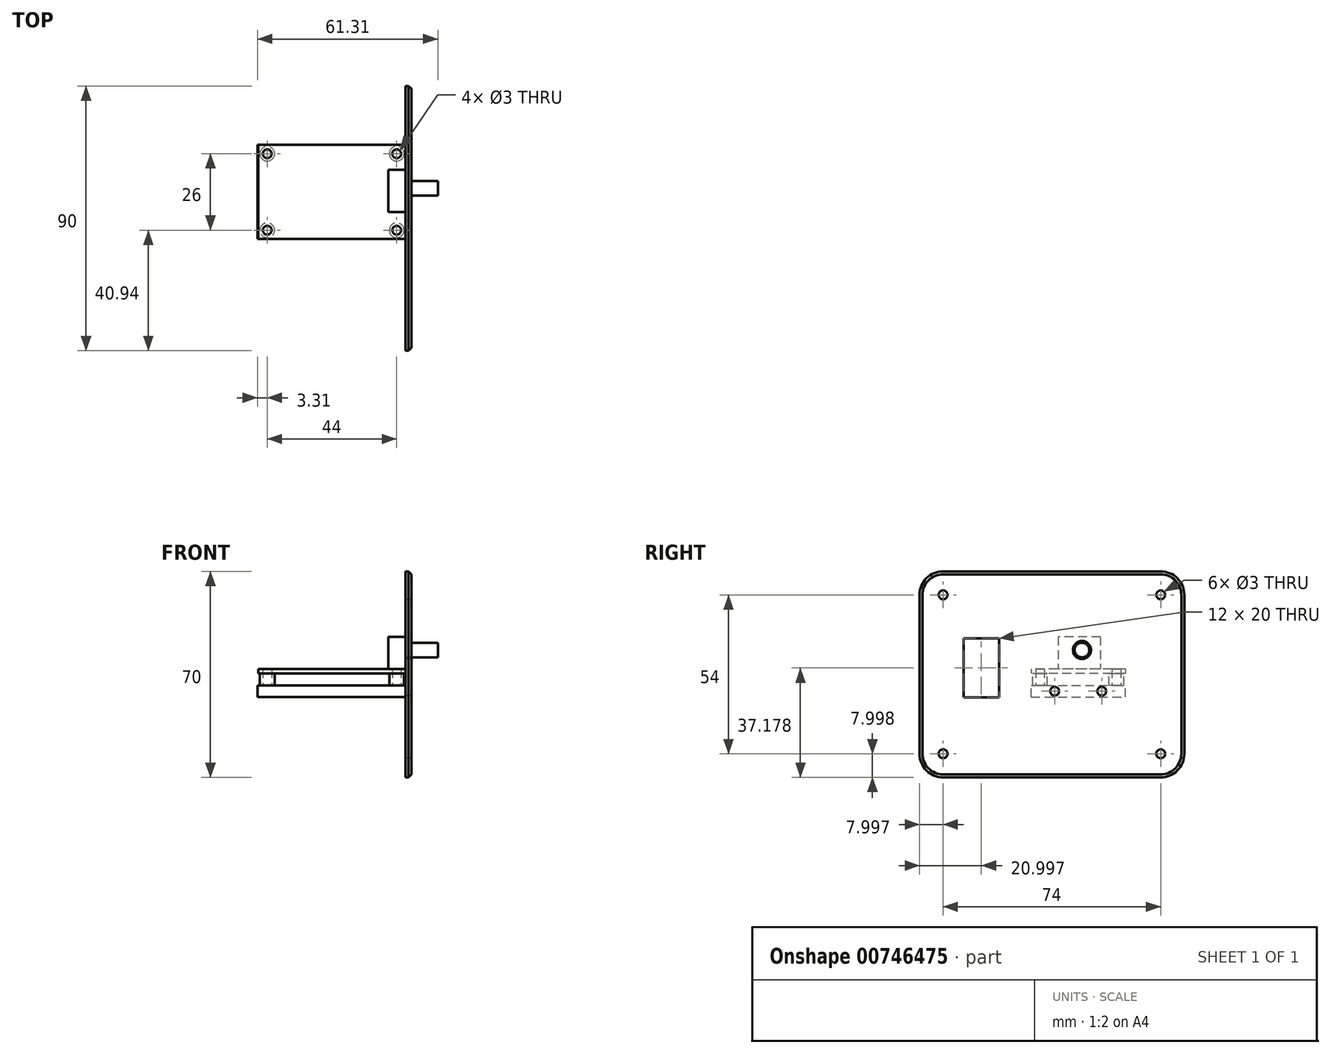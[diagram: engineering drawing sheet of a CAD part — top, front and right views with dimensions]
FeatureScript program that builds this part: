
annotation { "Feature Type Name" : "Feature", "Feature Type Description" : "" }
export const myFeature = defineFeature(function(context is Context, id is Id, definition is map)
    precondition{}
    {
        {
            var Q0;
            Q0=qCreatedBy(makeId("Top.planeOp"),FACE);
            var sketch = newSketch(context, id + "F0", { "sketchPlane" : qUnion([Q0])});
            skLineSegment(sketch, "E0.bottom", {"start": v(-13.65, 14.73) * mm, "end": v(36.35, 14.73) * mm});
            skLineSegment(sketch, "E0.top", {"start": v(-13.65, -17.27) * mm, "end": v(36.35, -17.27) * mm});
            skLineSegment(sketch, "E0.left", {"start": v(-13.65, 14.73) * mm, "end": v(-13.65, -17.27) * mm});
            skLineSegment(sketch, "E0.right", {"start": v(36.35, 14.73) * mm, "end": v(36.35, -17.27) * mm});
            skCircle(sketch, "E1", {"center": v(-10.65, 11.73) * mm, "radius": 1.5 * mm});
            skCircle(sketch, "E2", {"center": v(33.35, 11.73) * mm, "radius": 1.5 * mm});
            skCircle(sketch, "E3.0.1.0", {"center": v(-10.65, -14.27) * mm, "radius": 1.5 * mm});
            skCircle(sketch, "E3.0.1.1", {"center": v(33.35, -14.27) * mm, "radius": 1.5 * mm});
            skLineSegment(sketch, "E3.direction1", {"start": v(-10.65, 11.73) * mm, "end": v(12.25, 11.73) * mm, "construction": true});
            skLineSegment(sketch, "E3.direction2", {"start": v(-10.65, 11.73) * mm, "end": v(-10.65, -14.27) * mm, "construction": true});
            skSolve(sketch);
        }
        {
            var Q0;
            Q0=makeQuery(id+"F0.imprint","IMPRINT",FACE,{"disambiguationData":[TD([[makeQuery(id+"F0.imprint","IMPRINT",EDGE,{"derivedFrom":sQuery(id+"F0.wireOp",EDGE,"E0.bottom")}),-1.0]])]});
            extrude(context, id + "F1", {"entities" : qUnion([Q0]), "depth" : 1.5 * mm, "offsetDistance" : 25 * mm});
        }
        {
            var Q0;
            Q0=makeQuery(id+"F1.opExtrude","CAP_FACE",FACE,{"disambiguationData":[OSD([sQuery(id+"F0.wireOp",EDGE,"E0.bottom"),sQuery(id+"F0.wireOp",EDGE,"E0.top"),sQuery(id+"F0.wireOp",EDGE,"E0.left"),sQuery(id+"F0.wireOp",EDGE,"E0.right"),sQuery(id+"F0.wireOp",EDGE,"E1"),sQuery(id+"F0.wireOp",EDGE,"E2"),sQuery(id+"F0.wireOp",EDGE,"E3.0.1.0"),sQuery(id+"F0.wireOp",EDGE,"E3.0.1.1")])],"isStart":false});
            var sketch = newSketch(context, id + "F2", { "sketchPlane" : qUnion([Q0])});
            skLineSegment(sketch, "E4.bottom", {"start": v(36.35, 6.31) * mm, "end": v(30.58, 6.31) * mm});
            skLineSegment(sketch, "E4.top", {"start": v(36.35, -8.08) * mm, "end": v(30.58, -8.08) * mm});
            skLineSegment(sketch, "E4.left", {"start": v(36.35, 6.31) * mm, "end": v(36.35, -8.08) * mm});
            skLineSegment(sketch, "E4.right", {"start": v(30.58, 6.31) * mm, "end": v(30.58, -8.08) * mm});
            skSolve(sketch);
        }
        {
            var Q0;
            Q0 = qSketchRegion(id + "F2", true);
            extrude(context, id + "F3", {"entities" : qUnion([Q0]), "operationType" : NewBodyOperationType.ADD, "depth" : 11 * mm, "offsetDistance" : 25 * mm});
        }
        {
            var Q0;
            Q0=makeQuery(id+"F3.boolean.opBoolean","MERGE",FACE,{"derivedFrom":[makeQuery(id+"F1.opExtrude","SWEPT_FACE",FACE,{"disambiguationData":[OSD([sQuery(id+"F0.wireOp",EDGE,"E0.right")])]}),makeQuery(id+"F3.opExtrude","SWEPT_FACE",FACE,{"disambiguationData":[OSD([sQuery(id+"F2.wireOp",EDGE,"E4.left")])]})]});
            var sketch = newSketch(context, id + "F4", { "sketchPlane" : qUnion([Q0])});
            skCircle(sketch, "E5", {"center": v(0, 8) * mm, "radius": 2.5 * mm});
            skSolve(sketch);
        }
        {
            var Q0;
            Q0 = qSketchRegion(id + "F4", true);
            extrude(context, id + "F5", {"entities" : qUnion([Q0]), "operationType" : NewBodyOperationType.ADD, "depth" : 11 * mm, "offsetDistance" : 25 * mm});
        }
        {
            var Q0;
            Q0=makeQuery(id+"F1.opExtrude","CAP_FACE",FACE,{"disambiguationData":[OSD([sQuery(id+"F0.wireOp",EDGE,"E0.bottom"),sQuery(id+"F0.wireOp",EDGE,"E0.top"),sQuery(id+"F0.wireOp",EDGE,"E0.left"),sQuery(id+"F0.wireOp",EDGE,"E0.right"),sQuery(id+"F0.wireOp",EDGE,"E1"),sQuery(id+"F0.wireOp",EDGE,"E2"),sQuery(id+"F0.wireOp",EDGE,"E3.0.1.0"),sQuery(id+"F0.wireOp",EDGE,"E3.0.1.1")])],"isStart":true});
            var sketch = newSketch(context, id + "F6", { "sketchPlane" : qUnion([Q0])});
            skCircle(sketch, "E6", {"center": v(-10.65, 14.27) * mm, "radius": 2.5 * mm});
            skCircle(sketch, "E7", {"center": v(-10.65, -11.73) * mm, "radius": 2.5 * mm});
            skCircle(sketch, "E8", {"center": v(33.35, -11.73) * mm, "radius": 2.5 * mm});
            skCircle(sketch, "E9", {"center": v(33.35, 14.27) * mm, "radius": 2.5 * mm});
            skCircle(sketch, "E10", {"center": v(33.35, 14.27) * mm, "radius": 1.5 * mm});
            skCircle(sketch, "E11", {"center": v(-10.65, 14.27) * mm, "radius": 1.5 * mm});
            skCircle(sketch, "E12", {"center": v(-10.65, -11.73) * mm, "radius": 1.5 * mm});
            skCircle(sketch, "E13", {"center": v(33.35, -11.73) * mm, "radius": 1.5 * mm});
            skSolve(sketch);
        }
        {
            var Q0;
            Q0 = qSketchRegion(id + "F6", true);
            extrude(context, id + "F7", {"entities" : qUnion([Q0]), "operationType" : NewBodyOperationType.ADD, "depth" : 4 * mm, "offsetDistance" : 25 * mm});
        }
        {
            var Q0;
            Q0=makeQuery(id+"F7.opExtrude","CAP_FACE",FACE,{"disambiguationData":[OSD([sQuery(id+"F6.wireOp",EDGE,"E6"),sQuery(id+"F6.wireOp",EDGE,"E11")])],"isStart":false});
            var sketch = newSketch(context, id + "F8", { "sketchPlane" : qUnion([Q0])});
            skLineSegment(sketch, "E14.bottom", {"start": v(-13.96, 17.27) * mm, "end": v(36.35, 17.27) * mm});
            skLineSegment(sketch, "E14.top", {"start": v(-13.96, -14.73) * mm, "end": v(36.35, -14.73) * mm});
            skLineSegment(sketch, "E14.left", {"start": v(-13.96, 17.27) * mm, "end": v(-13.96, -14.73) * mm});
            skLineSegment(sketch, "E14.right", {"start": v(36.35, 17.27) * mm, "end": v(36.35, -14.73) * mm});
            skSolve(sketch);
        }
        {
            var Q0;
            Q0 = qSketchRegion(id + "F8", true);
            extrude(context, id + "F9", {"entities" : qUnion([Q0]), "depth" : 4 * mm, "offsetDistance" : 25 * mm});
        }
        {
            var Q0;
            Q0=makeQuery(id+"F9.opExtrude","SWEPT_FACE",FACE,{"disambiguationData":[OSD([sQuery(id+"F8.wireOp",EDGE,"E14.right")])]});
            var sketch = newSketch(context, id + "F10", { "sketchPlane" : qUnion([Q0])});
            skLineSegment(sketch, "E15.bottom", {"start": v(-47.21, 34.73) * mm, "end": v(26.79, 34.73) * mm});
            skLineSegment(sketch, "E15.top", {"start": v(-47.21, -35.27) * mm, "end": v(26.79, -35.27) * mm});
            skLineSegment(sketch, "E15.left", {"start": v(-55.21, 26.73) * mm, "end": v(-55.21, -27.27) * mm});
            skLineSegment(sketch, "E15.right", {"start": v(34.79, 26.73) * mm, "end": v(34.79, -27.27) * mm});
            skCircle(sketch, "E16", {"center": v(0, 8) * mm, "radius": 3.07 * mm});
            skLineSegment(sketch, "E17.bottom", {"start": v(-40.21, 11.9) * mm, "end": v(-28.21, 11.9) * mm});
            skLineSegment(sketch, "E17.top", {"start": v(-40.21, -8.1) * mm, "end": v(-28.21, -8.1) * mm});
            skLineSegment(sketch, "E17.left", {"start": v(-40.21, 11.9) * mm, "end": v(-40.21, -8.1) * mm});
            skLineSegment(sketch, "E17.right", {"start": v(-28.21, 11.9) * mm, "end": v(-28.21, -8.1) * mm});
            skPoint(sketch, "E18.visualSharp", {"position": v(-55.21, 34.73) * mm});
            skArc(sketch, "E18.filletArc", {"start": v(-47.21, 34.73) * mm, "mid": v(-52.87, 32.39) * mm, "end": v(-55.21, 26.73) * mm});
            skPoint(sketch, "E19.visualSharp", {"position": v(34.79, 34.73) * mm});
            skArc(sketch, "E19.filletArc", {"start": v(34.79, 26.73) * mm, "mid": v(32.44, 32.39) * mm, "end": v(26.79, 34.73) * mm});
            skPoint(sketch, "E20.visualSharp", {"position": v(34.79, -35.27) * mm});
            skArc(sketch, "E20.filletArc", {"start": v(26.79, -35.27) * mm, "mid": v(32.44, -32.93) * mm, "end": v(34.79, -27.27) * mm});
            skPoint(sketch, "E21.visualSharp", {"position": v(-55.21, -35.27) * mm});
            skArc(sketch, "E21.filletArc", {"start": v(-55.21, -27.27) * mm, "mid": v(-52.87, -32.93) * mm, "end": v(-47.21, -35.27) * mm});
            skCircle(sketch, "E22", {"center": v(-47.21, -27.27) * mm, "radius": 1.5 * mm});
            skCircle(sketch, "E23", {"center": v(-47.21, 26.73) * mm, "radius": 1.5 * mm});
            skCircle(sketch, "E24", {"center": v(26.79, 26.73) * mm, "radius": 1.5 * mm});
            skCircle(sketch, "E25", {"center": v(26.79, -27.27) * mm, "radius": 1.5 * mm});
            skCircle(sketch, "E26", {"center": v(-9.27, -6) * mm, "radius": 1.5 * mm});
            skCircle(sketch, "E27", {"center": v(6.73, -6) * mm, "radius": 1.5 * mm});
            skSolve(sketch);
        }
        {
            var Q0;
            Q0 = qSketchRegion(id + "F10", true);
            extrude(context, id + "F11", {"entities" : qUnion([Q0]), "depth" : 2 * mm, "offsetDistance" : 25 * mm});
        }
        {
            var Q0;
            Q0=makeQuery(id+"F11.opExtrude","CAP_EDGE",EDGE,{"disambiguationData":[OSD([sQuery(id+"F10.wireOp",EDGE,"E15.left")])],"isStart":false});
            chamfer(context, id + "F12", {"entities" : qUnion([Q0]), "width" : 1 * mm, "tangentPropagation" : true});
        }
    });
